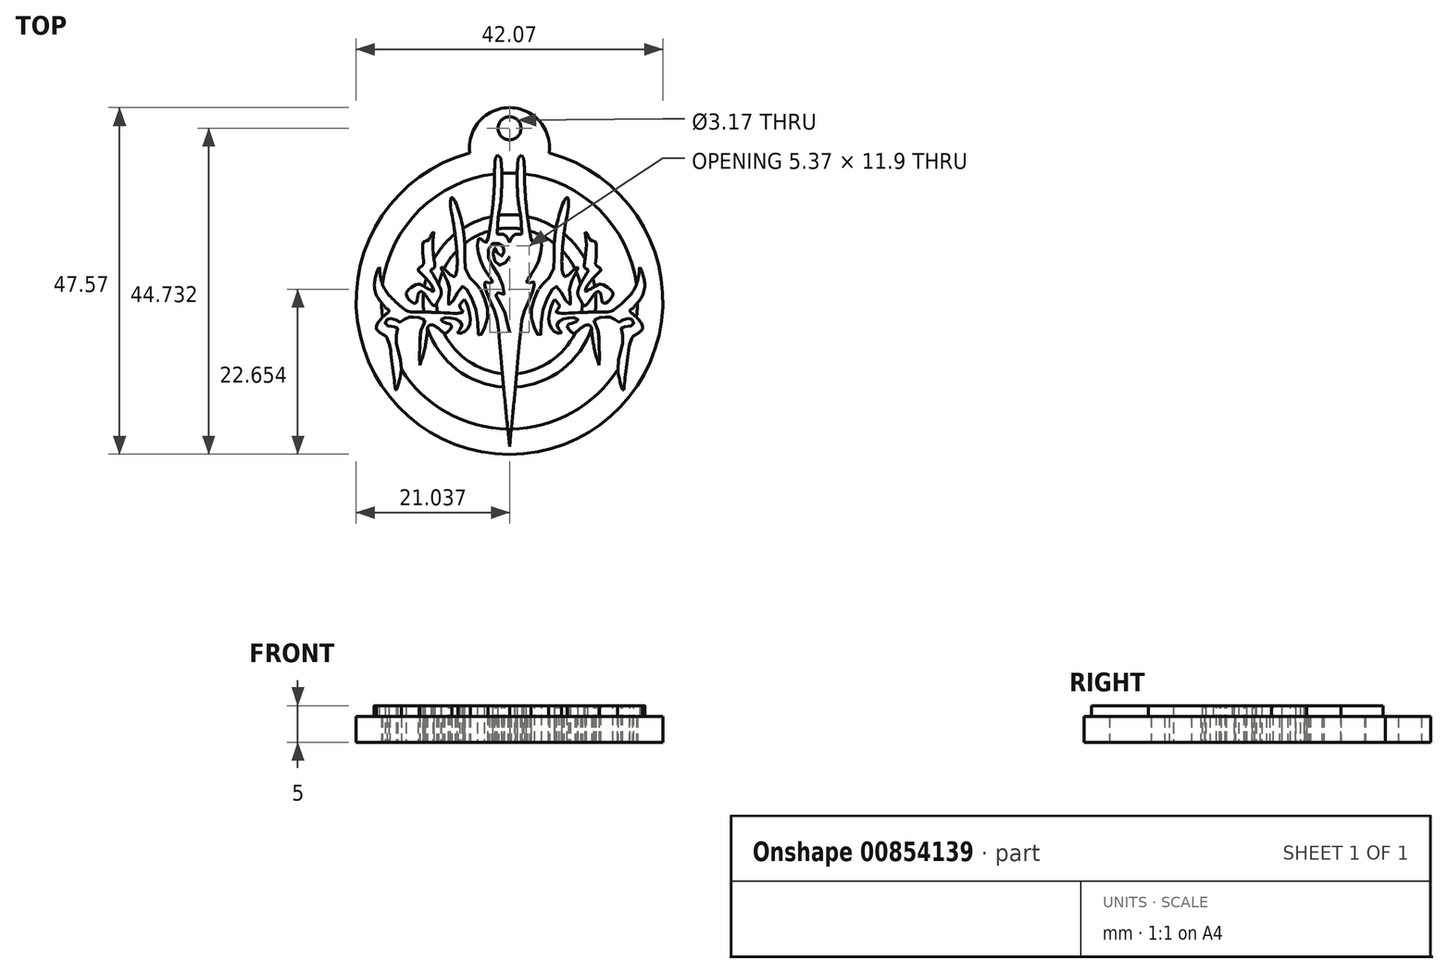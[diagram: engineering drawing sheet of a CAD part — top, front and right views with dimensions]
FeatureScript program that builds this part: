
annotation { "Feature Type Name" : "Feature", "Feature Type Description" : "" }
export const myFeature = defineFeature(function(context is Context, id is Id, definition is map)
    precondition{}
    {
        {
            var Q0;
            Q0=qCreatedBy(makeId("Top.planeOp"),FACE);
            var sketch = newSketch(context, id + "F0", { "sketchPlane" : qUnion([Q0])});
            skFitSpline(sketch, "E0", {"points": [v(-5.14, 14.8) * mm, v(-5.4, 14.38) * mm, v(-5.55, 11.82) * mm, v(-5.83, 7.5) * mm, v(-6.33, 3.87) * mm, v(-6.63, 2.9) * mm, v(-6.94, 2.82) * mm, v(-7.2, 3.15) * mm, v(-7.44, 3.37) * mm, v(-7.68, 3.39) * mm, v(-7.82, 3.07) * mm, v(-7.84, 1.76) * mm, v(-7.18, -0.34) * mm, v(-6.43, -1.55) * mm, v(-5.97, -2.28) * mm, v(-5.8, -2.52) * mm, v(-6.07, -2.72) * mm, v(-6.37, -2.66) * mm, v(-6.88, -2.6) * mm, v(-6.92, -2.8) * mm, v(-6.55, -4.2) * mm, v(-5.42, -7) * mm, v(-4.94, -9.94) * mm, v(-4.3, -17.1) * mm, v(-3.5, -25.2) * mm], "startDerivative": vector(-11.69, -12.68) * mm, "endDerivative": vector(7.97, -78.3) * mm});
            skFitSpline(sketch, "E1", {"points": [v(-5.14, 14.8) * mm, v(-4.8, 14.52) * mm, v(-4.6, 13.56) * mm, v(-4.54, 11.56) * mm, v(-4.58, 10.05) * mm, v(-4.73, 8.2) * mm, v(-5.05, 6.24) * mm, v(-5.14, 4.76) * mm, v(-5.14, 3.99) * mm, v(-4.51, 3.99) * mm, v(-3.91, 3.65) * mm, v(-3.5, 2.81) * mm], "startDerivative": vector(6.82, -3.82) * mm, "endDerivative": vector(4.35, -11.2) * mm});
            skFitSpline(sketch, "E2", {"points": [v(-3.5, 0.9) * mm, v(-3.76, 0.33) * mm, v(-4.4, -0.11) * mm, v(-4.9, -0.28) * mm, v(-5.3, -0.05) * mm, v(-5.66, 0.6) * mm, v(-5.76, 1.5) * mm, v(-5.6, 2.07) * mm, v(-5.36, 2) * mm, v(-5.14, 1.5) * mm, v(-4.86, 1.05) * mm, v(-4.55, 0.94) * mm, v(-4.33, 1.18) * mm, v(-4.26, 1.58) * mm, v(-4.26, 1.92) * mm, v(-4.44, 2.33) * mm, v(-4.73, 2.58) * mm, v(-5.14, 2.75) * mm, v(-5.6, 2.75) * mm, v(-6.1, 2.48) * mm, v(-6.4, 1.8) * mm, v(-6.43, 0.8) * mm, v(-5.94, -0.23) * mm, v(-5.05, -1.65) * mm, v(-4.4, -3.14) * mm, v(-4.22, -4.26) * mm, v(-4.46, -4.24) * mm, v(-5.05, -4.06) * mm, v(-5.39, -4.07) * mm, v(-5.33, -4.47) * mm, v(-4.74, -5.53) * mm, v(-4.08, -7.02) * mm, v(-3.73, -8.42) * mm, v(-3.5, -9.52) * mm], "startDerivative": vector(-6.13, -20.85) * mm, "endDerivative": vector(6, -27.3) * mm});
            skFitSpline(sketch, "E3", {"points": [v(-11.43, 9) * mm, v(-10.87, 8.29) * mm, v(-10.26, 6.48) * mm, v(-9.82, 4.42) * mm, v(-9.6, 1.1) * mm, v(-9.58, -0.72) * mm, v(-8.81, -2.15) * mm, v(-7.89, -3.02) * mm, v(-7.4, -3.67) * mm, v(-6.88, -4.98) * mm, v(-6.47, -6.43) * mm, v(-6.55, -7.66) * mm, v(-6.94, -8.97) * mm, v(-7.32, -9.77) * mm, v(-7.66, -10.04) * mm, v(-7.82, -8.9) * mm, v(-8.09, -6.45) * mm, v(-8.9, -4.43) * mm, v(-9.58, -3.32) * mm, v(-9.86, -3.16) * mm, v(-10.26, -3.46) * mm, v(-10.85, -4.51) * mm, v(-11.47, -5.44) * mm, v(-11.8, -5.68) * mm, v(-11.86, -5.18) * mm, v(-11.78, -4.1) * mm, v(-11.76, -3.2) * mm, v(-12.36, -1.83) * mm, v(-12.82, -0.78) * mm, v(-12.82, -0.58) * mm, v(-12.62, -0.64) * mm, v(-12, -1.23) * mm, v(-11.11, -1.83) * mm, v(-10.79, -1.33) * mm, v(-10.7, 1.43) * mm, v(-11.33, 6.33) * mm, v(-11.62, 8.13) * mm, v(-11.43, 9) * mm]});
            skFitSpline(sketch, "E4", {"points": [v(-13.9, 4.28) * mm, v(-14.39, 3.5) * mm, v(-14.65, 3.16) * mm, v(-15.3, 2.9) * mm, v(-15.4, 2.15) * mm, v(-15.37, 0.88) * mm, v(-15.28, 0) * mm, v(-15.4, -0.32) * mm, v(-16.04, -0.85) * mm, v(-15.73, -1.3) * mm, v(-14.92, -2.1) * mm, v(-14.3, -2.91) * mm, v(-13.96, -3.53) * mm, v(-13.9, -3.85) * mm, v(-14.39, -3.65) * mm, v(-15.42, -3.1) * mm, v(-15.97, -2.86) * mm, v(-16.64, -3.13) * mm, v(-17.46, -3.77) * mm, v(-17.67, -4.25) * mm, v(-17.2, -5.12) * mm, v(-16.52, -5.5) * mm, v(-16.26, -5.38) * mm, v(-16.07, -4.52) * mm, v(-15.85, -3.97) * mm, v(-15.54, -3.92) * mm, v(-15.08, -4.33) * mm, v(-14.48, -5.16) * mm, v(-13.86, -5.84) * mm, v(-13.57, -5.62) * mm, v(-12.95, -4.54) * mm, v(-12.93, -3.6) * mm, v(-13.6, -2.22) * mm, v(-14.15, -1.28) * mm, v(-14.27, -1) * mm, v(-13.96, -0.75) * mm, v(-13.77, -0.56) * mm, v(-13.89, 0.7) * mm, v(-14.03, 2.36) * mm, v(-13.98, 3.35) * mm, v(-13.9, 4.28) * mm]});
            skFitSpline(sketch, "E5", {"points": [v(-9.7, -5.01) * mm, v(-10.28, -5.67) * mm, v(-10.25, -6.15) * mm, v(-9.9, -6.64) * mm, v(-10.1, -6.8) * mm, v(-12.05, -6.84) * mm, v(-16.04, -6.7) * mm, v(-17.55, -6.52) * mm, v(-19.32, -5.13) * mm, v(-20.4, -3.93) * mm, v(-21.08, -2.36) * mm, v(-21.34, -0.54) * mm], "startDerivative": vector(-9.87, -9.17) * mm, "endDerivative": vector(-1.5, 17.66) * mm});
            skFitSpline(sketch, "E6", {"points": [v(-21.34, -0.54) * mm, v(-21.57, -0.9) * mm, v(-21.84, -1.76) * mm, v(-22.04, -2.85) * mm, v(-21.83, -4.23) * mm, v(-20.98, -5.54) * mm, v(-20.44, -6.14) * mm, v(-20.11, -6.39) * mm, v(-20.04, -6.6) * mm, v(-20.3, -6.89) * mm, v(-21.13, -7.64) * mm, v(-21.63, -8.4) * mm, v(-21.73, -9.04) * mm, v(-21.34, -9.47) * mm, v(-20.76, -9.84) * mm, v(-20.46, -10.03) * mm, v(-19.97, -11.13) * mm, v(-19.69, -13.16) * mm, v(-19.42, -15.28) * mm, v(-19.23, -16.75) * mm, v(-19.1, -17.42) * mm, v(-18.9, -17.13) * mm, v(-18.6, -16.03) * mm, v(-18.35, -14.5) * mm, v(-18.6, -12.58) * mm, v(-18.95, -11.25) * mm, v(-19.02, -9.93) * mm, v(-18.85, -8.93) * mm, v(-18.82, -8.8) * mm, v(-19.6, -8.75) * mm, v(-20.32, -8.57) * mm, v(-20.56, -8.3) * mm, v(-20.47, -7.88) * mm, v(-20.25, -7.7) * mm, v(-19.98, -7.62) * mm, v(-19.46, -7.62) * mm, v(-18.98, -7.82) * mm, v(-18.55, -8.07) * mm, v(-18.35, -8.02) * mm, v(-17.75, -7.62) * mm, v(-17.26, -7.41) * mm, v(-17.14, -7.41) * mm, v(-16.44, -7.43) * mm, v(-15.85, -7.47) * mm, v(-15.33, -7.67) * mm, v(-15.1, -7.85) * mm, v(-15.2, -8.2) * mm, v(-15.66, -9.35) * mm, v(-15.74, -9.9) * mm, v(-15.84, -12.25) * mm, v(-15.8, -13.99) * mm], "startDerivative": vector(-15.58, -21.3) * mm, "endDerivative": vector(2.34, -51.45) * mm});
            skFitSpline(sketch, "E7", {"points": [v(-15.8, -13.99) * mm, v(-15.41, -12.83) * mm, v(-15.05, -11.37) * mm, v(-14.9, -10.31) * mm, v(-14.78, -9.49) * mm, v(-14.7, -8.81) * mm, v(-14.4, -8.5) * mm, v(-13.93, -8.53) * mm, v(-13.4, -8.84) * mm, v(-13.04, -9.13) * mm, v(-12.93, -9.24) * mm, v(-12.62, -9.5) * mm, v(-12.45, -9.67) * mm, v(-12.16, -9.6) * mm, v(-11.81, -9.32) * mm, v(-11.5, -8.93) * mm, v(-11.42, -8.6) * mm, v(-11.59, -8.4) * mm, v(-12.06, -8.25) * mm, v(-12.64, -8.03) * mm, v(-12.93, -7.93) * mm, v(-12.68, -7.57) * mm, v(-11.91, -7.47) * mm, v(-11.1, -7.63) * mm, v(-10.42, -7.92) * mm, v(-10.04, -8.37) * mm, v(-10.2, -8.97) * mm, v(-10.61, -9.52) * mm, v(-10.5, -9.64) * mm, v(-9.94, -9.58) * mm, v(-9.39, -9.17) * mm, v(-9.07, -8.65) * mm, v(-8.88, -7.97) * mm, v(-9, -6.9) * mm, v(-9.25, -5.9) * mm, v(-9.55, -5.15) * mm, v(-9.7, -5.01) * mm], "startDerivative": vector(9.82, 27.15) * mm, "endDerivative": vector(-9.26, 5.8) * mm});
            skFitSpline(sketch, "E8.MirrorCS", {"points": [v(-1.84, 14.8) * mm, v(-2.19, 14.52) * mm, v(-2.38, 13.56) * mm, v(-2.45, 11.56) * mm, v(-2.4, 10.05) * mm, v(-2.26, 8.2) * mm, v(-1.94, 6.24) * mm, v(-1.84, 4.76) * mm, v(-1.84, 3.99) * mm, v(-2.48, 3.99) * mm, v(-3.07, 3.65) * mm, v(-3.5, 2.81) * mm], "startDerivative": vector(-6.82, -3.82) * mm, "endDerivative": vector(-4.35, -11.2) * mm});
            skFitSpline(sketch, "E9.MirrorCS", {"points": [v(-1.84, 14.8) * mm, v(-1.58, 14.38) * mm, v(-1.44, 11.82) * mm, v(-1.16, 7.5) * mm, v(-0.65, 3.87) * mm, v(-0.35, 2.9) * mm, v(-0.05, 2.82) * mm, v(0.21, 3.15) * mm, v(0.45, 3.37) * mm, v(0.7, 3.39) * mm, v(0.84, 3.07) * mm, v(0.86, 1.76) * mm, v(0.2, -0.34) * mm, v(-0.55, -1.55) * mm, v(-1.02, -2.28) * mm, v(-1.18, -2.52) * mm, v(-0.92, -2.72) * mm, v(-0.61, -2.66) * mm, v(-0.11, -2.6) * mm, v(-0.07, -2.8) * mm, v(-0.43, -4.2) * mm, v(-1.56, -7) * mm, v(-2.05, -9.94) * mm, v(-2.7, -17.1) * mm, v(-3.5, -25.2) * mm], "startDerivative": vector(11.69, -12.68) * mm, "endDerivative": vector(-7.97, -78.3) * mm});
            skFitSpline(sketch, "E10.MirrorCS", {"points": [v(-3.5, 0.9) * mm, v(-3.23, 0.33) * mm, v(-2.58, -0.11) * mm, v(-2.08, -0.28) * mm, v(-1.7, -0.05) * mm, v(-1.32, 0.6) * mm, v(-1.23, 1.5) * mm, v(-1.4, 2.07) * mm, v(-1.62, 2) * mm, v(-1.84, 1.5) * mm, v(-2.13, 1.05) * mm, v(-2.44, 0.94) * mm, v(-2.66, 1.18) * mm, v(-2.73, 1.58) * mm, v(-2.73, 1.92) * mm, v(-2.55, 2.33) * mm, v(-2.26, 2.58) * mm, v(-1.84, 2.75) * mm, v(-1.4, 2.75) * mm, v(-0.9, 2.48) * mm, v(-0.58, 1.8) * mm, v(-0.56, 0.8) * mm, v(-1.05, -0.23) * mm, v(-1.94, -1.65) * mm, v(-2.6, -3.14) * mm, v(-2.76, -4.26) * mm, v(-2.52, -4.24) * mm, v(-1.94, -4.06) * mm, v(-1.6, -4.07) * mm, v(-1.66, -4.47) * mm, v(-2.25, -5.53) * mm, v(-2.9, -7.02) * mm, v(-3.25, -8.42) * mm, v(-3.5, -9.52) * mm], "startDerivative": vector(6.13, -20.85) * mm, "endDerivative": vector(-6, -27.3) * mm});
            skFitSpline(sketch, "E11.MirrorC", {"points": [v(4.45, 9) * mm, v(3.88, 8.29) * mm, v(3.28, 6.48) * mm, v(2.83, 4.42) * mm, v(2.61, 1.1) * mm, v(2.6, -0.72) * mm, v(1.83, -2.15) * mm, v(0.9, -3.02) * mm, v(0.41, -3.67) * mm, v(-0.1, -4.98) * mm, v(-0.51, -6.43) * mm, v(-0.43, -7.66) * mm, v(-0.05, -8.97) * mm, v(0.33, -9.77) * mm, v(0.68, -10.04) * mm, v(0.84, -8.9) * mm, v(1.1, -6.45) * mm, v(1.9, -4.43) * mm, v(2.6, -3.32) * mm, v(2.87, -3.16) * mm, v(3.28, -3.46) * mm, v(3.86, -4.51) * mm, v(4.49, -5.44) * mm, v(4.8, -5.68) * mm, v(4.87, -5.18) * mm, v(4.79, -4.1) * mm, v(4.77, -3.2) * mm, v(5.37, -1.83) * mm, v(5.84, -0.78) * mm, v(5.84, -0.58) * mm, v(5.64, -0.64) * mm, v(5.01, -1.23) * mm, v(4.12, -1.83) * mm, v(3.8, -1.33) * mm, v(3.72, 1.43) * mm, v(4.35, 6.33) * mm, v(4.63, 8.13) * mm, v(4.45, 9) * mm]});
            skFitSpline(sketch, "E12.MirrorC", {"points": [v(6.92, 4.28) * mm, v(7.4, 3.5) * mm, v(7.67, 3.16) * mm, v(8.31, 2.9) * mm, v(8.4, 2.15) * mm, v(8.39, 0.88) * mm, v(8.29, 0) * mm, v(8.4, -0.32) * mm, v(9.06, -0.85) * mm, v(8.74, -1.3) * mm, v(7.93, -2.1) * mm, v(7.3, -2.91) * mm, v(6.97, -3.53) * mm, v(6.92, -3.85) * mm, v(7.4, -3.65) * mm, v(8.43, -3.1) * mm, v(8.98, -2.86) * mm, v(9.66, -3.13) * mm, v(10.47, -3.77) * mm, v(10.69, -4.25) * mm, v(10.2, -5.12) * mm, v(9.54, -5.5) * mm, v(9.27, -5.38) * mm, v(9.08, -4.52) * mm, v(8.86, -3.97) * mm, v(8.55, -3.92) * mm, v(8.1, -4.33) * mm, v(7.5, -5.16) * mm, v(6.87, -5.84) * mm, v(6.59, -5.62) * mm, v(5.96, -4.54) * mm, v(5.94, -3.6) * mm, v(6.61, -2.22) * mm, v(7.16, -1.28) * mm, v(7.28, -1) * mm, v(6.97, -0.75) * mm, v(6.78, -0.56) * mm, v(6.9, 0.7) * mm, v(7.04, 2.36) * mm, v(7, 3.35) * mm, v(6.92, 4.28) * mm]});
            skFitSpline(sketch, "E13.MirrorCS", {"points": [v(2.72, -5.01) * mm, v(3.3, -5.67) * mm, v(3.26, -6.15) * mm, v(2.92, -6.64) * mm, v(3.12, -6.8) * mm, v(5.06, -6.84) * mm, v(9.05, -6.7) * mm, v(10.56, -6.52) * mm, v(12.33, -5.13) * mm, v(13.41, -3.93) * mm, v(14.1, -2.36) * mm, v(14.35, -0.54) * mm], "startDerivative": vector(9.87, -9.17) * mm, "endDerivative": vector(1.5, 17.66) * mm});
            skFitSpline(sketch, "E14.MirrorCS", {"points": [v(14.35, -0.54) * mm, v(14.58, -0.9) * mm, v(14.85, -1.76) * mm, v(15.05, -2.85) * mm, v(14.84, -4.23) * mm, v(14, -5.54) * mm, v(13.45, -6.14) * mm, v(13.13, -6.39) * mm, v(13.05, -6.6) * mm, v(13.3, -6.89) * mm, v(14.14, -7.64) * mm, v(14.65, -8.4) * mm, v(14.75, -9.04) * mm, v(14.35, -9.47) * mm, v(13.77, -9.84) * mm, v(13.47, -10.03) * mm, v(12.98, -11.13) * mm, v(12.7, -13.16) * mm, v(12.43, -15.28) * mm, v(12.24, -16.75) * mm, v(12.1, -17.42) * mm, v(11.92, -17.13) * mm, v(11.62, -16.03) * mm, v(11.36, -14.5) * mm, v(11.6, -12.58) * mm, v(11.97, -11.25) * mm, v(12.04, -9.93) * mm, v(11.87, -8.93) * mm, v(11.83, -8.8) * mm, v(12.6, -8.75) * mm, v(13.33, -8.57) * mm, v(13.57, -8.3) * mm, v(13.48, -7.88) * mm, v(13.26, -7.7) * mm, v(13, -7.62) * mm, v(12.47, -7.62) * mm, v(12, -7.82) * mm, v(11.56, -8.07) * mm, v(11.37, -8.02) * mm, v(10.76, -7.62) * mm, v(10.27, -7.41) * mm, v(10.16, -7.41) * mm, v(9.46, -7.43) * mm, v(8.87, -7.47) * mm, v(8.35, -7.67) * mm, v(8.11, -7.85) * mm, v(8.2, -8.2) * mm, v(8.67, -9.35) * mm, v(8.75, -9.9) * mm, v(8.85, -12.25) * mm, v(8.82, -13.99) * mm], "startDerivative": vector(15.58, -21.3) * mm, "endDerivative": vector(-2.34, -51.45) * mm});
            skFitSpline(sketch, "E15.MirrorCS", {"points": [v(8.82, -13.99) * mm, v(8.42, -12.83) * mm, v(8.07, -11.37) * mm, v(7.91, -10.31) * mm, v(7.8, -9.49) * mm, v(7.72, -8.81) * mm, v(7.4, -8.5) * mm, v(6.95, -8.53) * mm, v(6.42, -8.84) * mm, v(6.05, -9.13) * mm, v(5.94, -9.24) * mm, v(5.63, -9.5) * mm, v(5.46, -9.67) * mm, v(5.17, -9.6) * mm, v(4.82, -9.32) * mm, v(4.52, -8.93) * mm, v(4.43, -8.6) * mm, v(4.6, -8.4) * mm, v(5.07, -8.25) * mm, v(5.65, -8.03) * mm, v(5.94, -7.93) * mm, v(5.7, -7.57) * mm, v(4.92, -7.47) * mm, v(4.1, -7.63) * mm, v(3.43, -7.92) * mm, v(3.05, -8.37) * mm, v(3.2, -8.97) * mm, v(3.63, -9.52) * mm, v(3.51, -9.64) * mm, v(2.96, -9.58) * mm, v(2.4, -9.17) * mm, v(2.08, -8.65) * mm, v(1.9, -7.97) * mm, v(2, -6.9) * mm, v(2.27, -5.9) * mm, v(2.56, -5.15) * mm, v(2.72, -5.01) * mm], "startDerivative": vector(-9.82, 27.15) * mm, "endDerivative": vector(9.26, 5.8) * mm});
            skCircle(sketch, "E16", {"center": v(-3.5, -5.2) * mm, "radius": 11.85 * mm});
            skCircle(sketch, "E17", {"center": v(-3.5, -5.2) * mm, "radius": 10 * mm});
            skCircle(sketch, "E18", {"center": v(-3.5, -5.2) * mm, "radius": 21.04 * mm});
            skArc(sketch, "E19", {"start": v(-21.05, -5.46) * mm, "mid": v(-21, -6.44) * mm, "end": v(-20.91, -7.42) * mm});
            skArc(sketch, "E20.trimOffspring", {"start": v(-20.32, -10.22) * mm, "mid": v(-20.11, -10.86) * mm, "end": v(-19.89, -11.49) * mm});
            skArc(sketch, "E21.trimOffspring", {"start": v(-18.35, -14.56) * mm, "mid": v(13.66, -1.43) * mm, "end": v(-20.9, -2.93) * mm});
            skCircle(sketch, "E22", {"center": v(-3.5, 18.5) * mm, "radius": 1.59 * mm});
            skPoint(sketch, "E23.center.orphan", {"position": v(-3.5, 15.84) * mm});
            skArc(sketch, "E24.trimOffspring", {"start": v(1.96, 15.12) * mm, "mid": v(-3.5, 21.34) * mm, "end": v(-8.95, 15.12) * mm});
            skSolve(sketch);
        }
        {
            var Q0;
            Q0 = qSketchRegion(id + "F0", true);
            var Q1;
            {var subQ0=sQuery(id+"F0.wireOp",EDGE,"E16");var subQ1=sQuery(id+"F0.wireOp",EDGE,"E0");var subQ2=makeQuery(id+"F0.imprint","INTERSECT",VERTEX,{"disambiguationData":[OD(0.0)],"derivedFrom":[subQ1,subQ0]});Q1=makeQuery(id+"F0.imprint","IMPRINT",FACE,{"disambiguationData":[TD([[makeQuery(id+"F0.imprint","IMPRINT",EDGE,{"disambiguationData":[TD([[subQ2,-1.0]])],"derivedFrom":subQ1}),-1.0]])]});}
            var Q2;
            {var subQ0=sQuery(id+"F0.wireOp",EDGE,"E16");var subQ1=sQuery(id+"F0.wireOp",EDGE,"E1");var subQ2=makeQuery(id+"F0.imprint","INTERSECT",VERTEX,{"derivedFrom":[subQ1,subQ0]});Q2=makeQuery(id+"F0.imprint","IMPRINT",FACE,{"disambiguationData":[TD([[makeQuery(id+"F0.imprint","IMPRINT",EDGE,{"disambiguationData":[TD([[subQ2,-1.0]])],"derivedFrom":subQ1}),1.0]])]});}
            var Q3;
            {var subQ0=sQuery(id+"F0.wireOp",EDGE,"E16");var subQ1=sQuery(id+"F0.wireOp",EDGE,"E9.MirrorCS");var subQ2=makeQuery(id+"F0.imprint","INTERSECT",VERTEX,{"disambiguationData":[OD(0.0)],"derivedFrom":[subQ1,subQ0]});Q3=makeQuery(id+"F0.imprint","IMPRINT",FACE,{"disambiguationData":[TD([[makeQuery(id+"F0.imprint","IMPRINT",EDGE,{"disambiguationData":[TD([[subQ2,-1.0]])],"derivedFrom":subQ1}),1.0]])]});}
            var Q4;
            {var subQ1=sQuery(id+"F0.wireOp",EDGE,"E11.MirrorC");var subQ5=sQuery(id+"F0.wireOp",EDGE,"E17");var subQ8=makeQuery(id+"F0.imprint","INTERSECT",VERTEX,{"disambiguationData":[OD(1.0)],"derivedFrom":[subQ1,subQ5]});Q4=makeQuery(id+"F0.imprint","IMPRINT",FACE,{"disambiguationData":[TD([[makeQuery(id+"F0.imprint","IMPRINT",EDGE,{"disambiguationData":[TD([[subQ8,-1.0]])],"derivedFrom":subQ1}),-1.0]])]});}
            var Q5;
            {var subQ0=sQuery(id+"F0.wireOp",EDGE,"E16");var subQ1=sQuery(id+"F0.wireOp",EDGE,"E12.MirrorC");var subQ2=makeQuery(id+"F0.imprint","INTERSECT",VERTEX,{"disambiguationData":[OD(2.0)],"derivedFrom":[subQ1,subQ0]});Q5=makeQuery(id+"F0.imprint","IMPRINT",FACE,{"disambiguationData":[TD([[makeQuery(id+"F0.imprint","IMPRINT",EDGE,{"disambiguationData":[TD([[subQ2,-1.0]])],"derivedFrom":subQ1}),1.0]])]});}
            var Q6;
            {var subQ0=sQuery(id+"F0.wireOp",EDGE,"E17");var subQ1=sQuery(id+"F0.wireOp",EDGE,"E9.MirrorCS");var subQ2=makeQuery(id+"F0.imprint","INTERSECT",VERTEX,{"disambiguationData":[OD(1.0)],"derivedFrom":[subQ1,subQ0]});Q6=makeQuery(id+"F0.imprint","IMPRINT",FACE,{"disambiguationData":[TD([[makeQuery(id+"F0.imprint","IMPRINT",EDGE,{"disambiguationData":[TD([[subQ2,-1.0]])],"derivedFrom":subQ1}),1.0]])]});}
            var Q7;
            {var subQ0=sQuery(id+"F0.wireOp",EDGE,"E17");var subQ1=sQuery(id+"F0.wireOp",EDGE,"E0");var subQ2=makeQuery(id+"F0.imprint","INTERSECT",VERTEX,{"disambiguationData":[OD(1.0)],"derivedFrom":[subQ1,subQ0]});Q7=makeQuery(id+"F0.imprint","IMPRINT",FACE,{"disambiguationData":[TD([[makeQuery(id+"F0.imprint","IMPRINT",EDGE,{"disambiguationData":[TD([[subQ2,-1.0]])],"derivedFrom":subQ1}),-1.0]])]});}
            var Q8;
            {var subQ0=sQuery(id+"F0.wireOp",EDGE,"E16");var subQ1=sQuery(id+"F0.wireOp",EDGE,"E4");var subQ2=makeQuery(id+"F0.imprint","INTERSECT",VERTEX,{"disambiguationData":[OD(2.0)],"derivedFrom":[subQ1,subQ0]});Q8=makeQuery(id+"F0.imprint","IMPRINT",FACE,{"disambiguationData":[TD([[makeQuery(id+"F0.imprint","IMPRINT",EDGE,{"disambiguationData":[TD([[subQ2,-1.0]])],"derivedFrom":subQ1}),-1.0]])]});}
            var Q9;
            {var subQ0=sQuery(id+"F0.wireOp",EDGE,"E16");var subQ1=sQuery(id+"F0.wireOp",EDGE,"E4");var subQ2=makeQuery(id+"F0.imprint","INTERSECT",VERTEX,{"disambiguationData":[OD(0.0)],"derivedFrom":[subQ1,subQ0]});Q9=makeQuery(id+"F0.imprint","IMPRINT",FACE,{"disambiguationData":[TD([[makeQuery(id+"F0.imprint","IMPRINT",EDGE,{"disambiguationData":[TD([[subQ2,1.0]])],"derivedFrom":subQ1}),-1.0]])]});}
            var Q10;
            {var subQ1=sQuery(id+"F0.wireOp",EDGE,"E3");var subQ5=sQuery(id+"F0.wireOp",EDGE,"E17");var subQ8=makeQuery(id+"F0.imprint","INTERSECT",VERTEX,{"disambiguationData":[OD(1.0)],"derivedFrom":[subQ1,subQ5]});Q10=makeQuery(id+"F0.imprint","IMPRINT",FACE,{"disambiguationData":[TD([[makeQuery(id+"F0.imprint","IMPRINT",EDGE,{"disambiguationData":[TD([[subQ8,-1.0]])],"derivedFrom":subQ1}),1.0]])]});}
            var Q11;
            {var subQ0=sQuery(id+"F0.wireOp",EDGE,"E16");var subQ1=sQuery(id+"F0.wireOp",EDGE,"E12.MirrorC");var subQ2=makeQuery(id+"F0.imprint","INTERSECT",VERTEX,{"disambiguationData":[OD(0.0)],"derivedFrom":[subQ1,subQ0]});Q11=makeQuery(id+"F0.imprint","IMPRINT",FACE,{"disambiguationData":[TD([[makeQuery(id+"F0.imprint","IMPRINT",EDGE,{"disambiguationData":[TD([[subQ2,1.0]])],"derivedFrom":subQ1}),1.0]])]});}
            extrude(context, id + "F1", {"entities" : qUnion([Q0, Q1, Q2, Q3, Q4, Q5, Q6, Q7, Q8, Q9, Q10, Q11]), "depth" : 3.5 * mm, "offsetDistance" : 25 * mm});
        }
        {
            var Q0;
            {var subQ0=sQuery(id+"F0.wireOp",EDGE,"E21.trimOffspring");var subQ1=sQuery(id+"F0.wireOp",EDGE,"E0");var subQ2=makeQuery(id+"F0.imprint","INTERSECT",VERTEX,{"disambiguationData":[OD(0.0)],"derivedFrom":[subQ1,subQ0]});Q0=makeQuery(id+"F0.imprint","IMPRINT",FACE,{"disambiguationData":[TD([[makeQuery(id+"F0.imprint","IMPRINT",EDGE,{"disambiguationData":[TD([[subQ2,-1.0]])],"derivedFrom":subQ1}),1.0]])]});}
            var Q1;
            {var subQ0=sQuery(id+"F0.wireOp",EDGE,"E1");var subQ1=sQuery(id+"F0.wireOp",EDGE,"E0");var subQ2=makeQuery(id+"F0.imprint","INTERSECT",VERTEX,{"derivedFrom":[subQ1,subQ0]});Q1=makeQuery(id+"F0.imprint","IMPRINT",FACE,{"disambiguationData":[TD([[makeQuery(id+"F0.imprint","IMPRINT",EDGE,{"disambiguationData":[TD([[subQ2,-1.0]])],"derivedFrom":subQ1}),1.0]])]});}
            var Q2;
            {var subQ0=sQuery(id+"F0.wireOp",EDGE,"E9.MirrorCS");var subQ1=sQuery(id+"F0.wireOp",EDGE,"E8.MirrorCS");var subQ2=makeQuery(id+"F0.imprint","INTERSECT",VERTEX,{"derivedFrom":[subQ1,subQ0]});Q2=makeQuery(id+"F0.imprint","IMPRINT",FACE,{"disambiguationData":[TD([[makeQuery(id+"F0.imprint","IMPRINT",EDGE,{"disambiguationData":[TD([[subQ2,-1.0]])],"derivedFrom":subQ1}),1.0]])]});}
            var Q3;
            {var subQ0=sQuery(id+"F0.wireOp",EDGE,"E21.trimOffspring");var subQ1=sQuery(id+"F0.wireOp",EDGE,"E8.MirrorCS");var subQ2=makeQuery(id+"F0.imprint","INTERSECT",VERTEX,{"derivedFrom":[subQ1,subQ0]});Q3=makeQuery(id+"F0.imprint","IMPRINT",FACE,{"disambiguationData":[TD([[makeQuery(id+"F0.imprint","IMPRINT",EDGE,{"disambiguationData":[TD([[subQ2,-1.0]])],"derivedFrom":subQ1}),1.0]])]});}
            var Q4;
            {var subQ0=sQuery(id+"F0.wireOp",EDGE,"E16");var subQ1=sQuery(id+"F0.wireOp",EDGE,"E0");var subQ2=makeQuery(id+"F0.imprint","INTERSECT",VERTEX,{"disambiguationData":[OD(0.0)],"derivedFrom":[subQ1,subQ0]});Q4=makeQuery(id+"F0.imprint","IMPRINT",FACE,{"disambiguationData":[TD([[makeQuery(id+"F0.imprint","IMPRINT",EDGE,{"disambiguationData":[TD([[subQ2,-1.0]])],"derivedFrom":subQ1}),1.0]])]});}
            var Q5;
            Q5=makeQuery(id+"F0.imprint","IMPRINT",FACE,{"disambiguationData":[TD([[makeQuery(id+"F0.imprint","IMPRINT",EDGE,{"derivedFrom":sQuery(id+"F0.wireOp",EDGE,"E2")}),-1.0]])]});
            var Q6;
            {var subQ0=sQuery(id+"F0.wireOp",EDGE,"E16");var subQ1=sQuery(id+"F0.wireOp",EDGE,"E8.MirrorCS");var subQ2=makeQuery(id+"F0.imprint","INTERSECT",VERTEX,{"derivedFrom":[subQ1,subQ0]});Q6=makeQuery(id+"F0.imprint","IMPRINT",FACE,{"disambiguationData":[TD([[makeQuery(id+"F0.imprint","IMPRINT",EDGE,{"disambiguationData":[TD([[subQ2,-1.0]])],"derivedFrom":subQ1}),1.0]])]});}
            var Q7;
            {var subQ0=sQuery(id+"F0.wireOp",EDGE,"E17");var subQ1=sQuery(id+"F0.wireOp",EDGE,"E5");var subQ2=makeQuery(id+"F0.imprint","INTERSECT",VERTEX,{"derivedFrom":[subQ1,subQ0]});Q7=makeQuery(id+"F0.imprint","IMPRINT",FACE,{"disambiguationData":[TD([[makeQuery(id+"F0.imprint","IMPRINT",EDGE,{"disambiguationData":[TD([[subQ2,-1.0]])],"derivedFrom":subQ1}),1.0]])]});}
            var Q8;
            {var subQ0=sQuery(id+"F0.wireOp",EDGE,"E7");var subQ1=sQuery(id+"F0.wireOp",EDGE,"E5");var subQ2=makeQuery(id+"F0.imprint","INTERSECT",VERTEX,{"derivedFrom":[subQ1,subQ0]});Q8=makeQuery(id+"F0.imprint","IMPRINT",FACE,{"disambiguationData":[TD([[makeQuery(id+"F0.imprint","IMPRINT",EDGE,{"disambiguationData":[TD([[subQ2,-1.0]])],"derivedFrom":subQ1}),1.0]])]});}
            var Q9;
            {var subQ4=sQuery(id+"F0.wireOp",EDGE,"E5");var subQ6=sQuery(id+"F0.wireOp",EDGE,"E21.trimOffspring");var subQ7=makeQuery(id+"F0.imprint","INTERSECT",VERTEX,{"derivedFrom":[subQ4,subQ6]});Q9=makeQuery(id+"F0.imprint","IMPRINT",FACE,{"disambiguationData":[TD([[makeQuery(id+"F0.imprint","IMPRINT",EDGE,{"disambiguationData":[TD([[subQ7,1.0]])],"derivedFrom":subQ4}),1.0]])]});}
            var Q10;
            {var subQ0=sQuery(id+"F0.wireOp",EDGE,"E16");var subQ1=sQuery(id+"F0.wireOp",EDGE,"E4");var subQ2=makeQuery(id+"F0.imprint","INTERSECT",VERTEX,{"disambiguationData":[OD(0.0)],"derivedFrom":[subQ1,subQ0]});Q10=makeQuery(id+"F0.imprint","IMPRINT",FACE,{"disambiguationData":[TD([[makeQuery(id+"F0.imprint","IMPRINT",EDGE,{"disambiguationData":[TD([[subQ2,-1.0]])],"derivedFrom":subQ1}),1.0]])]});}
            var Q11;
            {var subQ0=sQuery(id+"F0.wireOp",EDGE,"E16");var subQ1=sQuery(id+"F0.wireOp",EDGE,"E4");var subQ2=makeQuery(id+"F0.imprint","INTERSECT",VERTEX,{"disambiguationData":[OD(1.0)],"derivedFrom":[subQ1,subQ0]});Q11=makeQuery(id+"F0.imprint","IMPRINT",FACE,{"disambiguationData":[TD([[makeQuery(id+"F0.imprint","IMPRINT",EDGE,{"disambiguationData":[TD([[subQ2,1.0]])],"derivedFrom":subQ1}),1.0]])]});}
            var Q12;
            {var subQ0=sQuery(id+"F0.wireOp",EDGE,"E17");var subQ1=sQuery(id+"F0.wireOp",EDGE,"E0");var subQ2=makeQuery(id+"F0.imprint","INTERSECT",VERTEX,{"disambiguationData":[OD(1.0)],"derivedFrom":[subQ1,subQ0]});Q12=makeQuery(id+"F0.imprint","IMPRINT",FACE,{"disambiguationData":[TD([[makeQuery(id+"F0.imprint","IMPRINT",EDGE,{"disambiguationData":[TD([[subQ2,-1.0]])],"derivedFrom":subQ1}),1.0]])]});}
            var Q13;
            {var subQ0=sQuery(id+"F0.wireOp",EDGE,"E16");var subQ1=sQuery(id+"F0.wireOp",EDGE,"E0");var subQ2=makeQuery(id+"F0.imprint","INTERSECT",VERTEX,{"disambiguationData":[OD(1.0)],"derivedFrom":[subQ1,subQ0]});Q13=makeQuery(id+"F0.imprint","IMPRINT",FACE,{"disambiguationData":[TD([[makeQuery(id+"F0.imprint","IMPRINT",EDGE,{"disambiguationData":[TD([[subQ2,-1.0]])],"derivedFrom":subQ1}),1.0]])]});}
            var Q14;
            {var subQ0=sQuery(id+"F0.wireOp",EDGE,"E9.MirrorCS");var subQ1=sQuery(id+"F0.wireOp",EDGE,"E0");var subQ2=makeQuery(id+"F0.imprint","INTERSECT",VERTEX,{"derivedFrom":[subQ1,subQ0]});Q14=makeQuery(id+"F0.imprint","IMPRINT",FACE,{"disambiguationData":[TD([[makeQuery(id+"F0.imprint","IMPRINT",EDGE,{"disambiguationData":[TD([[subQ2,1.0]])],"derivedFrom":subQ1}),1.0]])]});}
            var Q15;
            {var subQ0=sQuery(id+"F0.wireOp",EDGE,"E21.trimOffspring");var subQ1=sQuery(id+"F0.wireOp",EDGE,"E14.MirrorCS");var subQ2=makeQuery(id+"F0.imprint","INTERSECT",VERTEX,{"disambiguationData":[OD(3.0)],"derivedFrom":[subQ1,subQ0]});Q15=makeQuery(id+"F0.imprint","IMPRINT",FACE,{"disambiguationData":[TD([[makeQuery(id+"F0.imprint","IMPRINT",EDGE,{"disambiguationData":[TD([[subQ2,-1.0]])],"derivedFrom":subQ1}),-1.0]])]});}
            var Q16;
            {var subQ9=sQuery(id+"F0.wireOp",EDGE,"E16");var subQ10=sQuery(id+"F0.wireOp",EDGE,"E13.MirrorCS");var subQ11=makeQuery(id+"F0.imprint","INTERSECT",VERTEX,{"derivedFrom":[subQ10,subQ9]});Q16=makeQuery(id+"F0.imprint","IMPRINT",FACE,{"disambiguationData":[TD([[makeQuery(id+"F0.imprint","IMPRINT",EDGE,{"disambiguationData":[TD([[subQ11,-1.0]])],"derivedFrom":subQ10}),-1.0]])]});}
            var Q17;
            {var subQ0=sQuery(id+"F0.wireOp",EDGE,"E14.MirrorCS");var subQ1=sQuery(id+"F0.wireOp",EDGE,"E13.MirrorCS");var subQ2=makeQuery(id+"F0.imprint","INTERSECT",VERTEX,{"derivedFrom":[subQ1,subQ0]});Q17=makeQuery(id+"F0.imprint","IMPRINT",FACE,{"disambiguationData":[TD([[makeQuery(id+"F0.imprint","IMPRINT",EDGE,{"disambiguationData":[TD([[subQ2,1.0]])],"derivedFrom":subQ1}),-1.0]])]});}
            var Q18;
            {var subQ0=sQuery(id+"F0.wireOp",EDGE,"E21.trimOffspring");var subQ1=sQuery(id+"F0.wireOp",EDGE,"E14.MirrorCS");var subQ2=makeQuery(id+"F0.imprint","INTERSECT",VERTEX,{"disambiguationData":[OD(1.0)],"derivedFrom":[subQ1,subQ0]});Q18=makeQuery(id+"F0.imprint","IMPRINT",FACE,{"disambiguationData":[TD([[makeQuery(id+"F0.imprint","IMPRINT",EDGE,{"disambiguationData":[TD([[subQ2,-1.0]])],"derivedFrom":subQ1}),-1.0]])]});}
            var Q19;
            {var subQ0=sQuery(id+"F0.wireOp",EDGE,"E17");var subQ1=sQuery(id+"F0.wireOp",EDGE,"E13.MirrorCS");var subQ2=makeQuery(id+"F0.imprint","INTERSECT",VERTEX,{"derivedFrom":[subQ1,subQ0]});Q19=makeQuery(id+"F0.imprint","IMPRINT",FACE,{"disambiguationData":[TD([[makeQuery(id+"F0.imprint","IMPRINT",EDGE,{"disambiguationData":[TD([[subQ2,-1.0]])],"derivedFrom":subQ1}),-1.0]])]});}
            var Q20;
            {var subQ0=sQuery(id+"F0.wireOp",EDGE,"E16");var subQ1=sQuery(id+"F0.wireOp",EDGE,"E12.MirrorC");var subQ2=makeQuery(id+"F0.imprint","INTERSECT",VERTEX,{"disambiguationData":[OD(0.0)],"derivedFrom":[subQ1,subQ0]});Q20=makeQuery(id+"F0.imprint","IMPRINT",FACE,{"disambiguationData":[TD([[makeQuery(id+"F0.imprint","IMPRINT",EDGE,{"disambiguationData":[TD([[subQ2,1.0]])],"derivedFrom":subQ1}),-1.0]])]});}
            var Q21;
            {var subQ0=sQuery(id+"F0.wireOp",EDGE,"E16");var subQ1=sQuery(id+"F0.wireOp",EDGE,"E12.MirrorC");var subQ2=makeQuery(id+"F0.imprint","INTERSECT",VERTEX,{"disambiguationData":[OD(0.0)],"derivedFrom":[subQ1,subQ0]});Q21=makeQuery(id+"F0.imprint","IMPRINT",FACE,{"disambiguationData":[TD([[makeQuery(id+"F0.imprint","IMPRINT",EDGE,{"disambiguationData":[TD([[subQ2,-1.0]])],"derivedFrom":subQ1}),-1.0]])]});}
            var Q22;
            {var subQ0=sQuery(id+"F0.wireOp",EDGE,"E16");var subQ1=sQuery(id+"F0.wireOp",EDGE,"E12.MirrorC");var subQ2=makeQuery(id+"F0.imprint","INTERSECT",VERTEX,{"disambiguationData":[OD(1.0)],"derivedFrom":[subQ1,subQ0]});Q22=makeQuery(id+"F0.imprint","IMPRINT",FACE,{"disambiguationData":[TD([[makeQuery(id+"F0.imprint","IMPRINT",EDGE,{"disambiguationData":[TD([[subQ2,1.0]])],"derivedFrom":subQ1}),-1.0]])]});}
            var Q23;
            {var subQ0=sQuery(id+"F0.wireOp",EDGE,"E17");var subQ1=sQuery(id+"F0.wireOp",EDGE,"E12.MirrorC");var subQ2=makeQuery(id+"F0.imprint","INTERSECT",VERTEX,{"disambiguationData":[OD(0.0)],"derivedFrom":[subQ1,subQ0]});Q23=makeQuery(id+"F0.imprint","IMPRINT",FACE,{"disambiguationData":[TD([[makeQuery(id+"F0.imprint","IMPRINT",EDGE,{"disambiguationData":[TD([[subQ2,-1.0]])],"derivedFrom":subQ1}),-1.0]])]});}
            var Q24;
            {var subQ0=sQuery(id+"F0.wireOp",EDGE,"E15.MirrorCS");var subQ1=sQuery(id+"F0.wireOp",EDGE,"E13.MirrorCS");var subQ2=makeQuery(id+"F0.imprint","INTERSECT",VERTEX,{"derivedFrom":[subQ1,subQ0]});Q24=makeQuery(id+"F0.imprint","IMPRINT",FACE,{"disambiguationData":[TD([[makeQuery(id+"F0.imprint","IMPRINT",EDGE,{"disambiguationData":[TD([[subQ2,-1.0]])],"derivedFrom":subQ1}),-1.0]])]});}
            var Q25;
            {var subQ0=sQuery(id+"F0.wireOp",EDGE,"E17");var subQ1=sQuery(id+"F0.wireOp",EDGE,"E11.MirrorC");var subQ2=makeQuery(id+"F0.imprint","INTERSECT",VERTEX,{"disambiguationData":[OD(0.0)],"derivedFrom":[subQ1,subQ0]});Q25=makeQuery(id+"F0.imprint","IMPRINT",FACE,{"disambiguationData":[TD([[makeQuery(id+"F0.imprint","IMPRINT",EDGE,{"disambiguationData":[TD([[subQ2,-1.0]])],"derivedFrom":subQ1}),1.0]])]});}
            var Q26;
            {var subQ0=sQuery(id+"F0.wireOp",EDGE,"E17");var subQ1=sQuery(id+"F0.wireOp",EDGE,"E11.MirrorC");var subQ2=makeQuery(id+"F0.imprint","INTERSECT",VERTEX,{"disambiguationData":[OD(0.0)],"derivedFrom":[subQ1,subQ0]});Q26=makeQuery(id+"F0.imprint","IMPRINT",FACE,{"disambiguationData":[TD([[makeQuery(id+"F0.imprint","IMPRINT",EDGE,{"disambiguationData":[TD([[subQ2,1.0]])],"derivedFrom":subQ1}),1.0]])]});}
            var Q27;
            {var subQ0=sQuery(id+"F0.wireOp",EDGE,"E16");var subQ1=sQuery(id+"F0.wireOp",EDGE,"E11.MirrorC");var subQ2=makeQuery(id+"F0.imprint","INTERSECT",VERTEX,{"disambiguationData":[OD(0.0)],"derivedFrom":[subQ1,subQ0]});Q27=makeQuery(id+"F0.imprint","IMPRINT",FACE,{"disambiguationData":[TD([[makeQuery(id+"F0.imprint","IMPRINT",EDGE,{"disambiguationData":[TD([[subQ2,1.0]])],"derivedFrom":subQ1}),1.0]])]});}
            var Q28;
            {var subQ0=sQuery(id+"F0.wireOp",EDGE,"E16");var subQ1=sQuery(id+"F0.wireOp",EDGE,"E3");var subQ2=makeQuery(id+"F0.imprint","INTERSECT",VERTEX,{"disambiguationData":[OD(0.0)],"derivedFrom":[subQ1,subQ0]});Q28=makeQuery(id+"F0.imprint","IMPRINT",FACE,{"disambiguationData":[TD([[makeQuery(id+"F0.imprint","IMPRINT",EDGE,{"disambiguationData":[TD([[subQ2,1.0]])],"derivedFrom":subQ1}),-1.0]])]});}
            var Q29;
            {var subQ0=sQuery(id+"F0.wireOp",EDGE,"E17");var subQ1=sQuery(id+"F0.wireOp",EDGE,"E3");var subQ2=makeQuery(id+"F0.imprint","INTERSECT",VERTEX,{"disambiguationData":[OD(0.0)],"derivedFrom":[subQ1,subQ0]});Q29=makeQuery(id+"F0.imprint","IMPRINT",FACE,{"disambiguationData":[TD([[makeQuery(id+"F0.imprint","IMPRINT",EDGE,{"disambiguationData":[TD([[subQ2,1.0]])],"derivedFrom":subQ1}),-1.0]])]});}
            var Q30;
            {var subQ0=sQuery(id+"F0.wireOp",EDGE,"E17");var subQ1=sQuery(id+"F0.wireOp",EDGE,"E3");var subQ2=makeQuery(id+"F0.imprint","INTERSECT",VERTEX,{"disambiguationData":[OD(0.0)],"derivedFrom":[subQ1,subQ0]});Q30=makeQuery(id+"F0.imprint","IMPRINT",FACE,{"disambiguationData":[TD([[makeQuery(id+"F0.imprint","IMPRINT",EDGE,{"disambiguationData":[TD([[subQ2,-1.0]])],"derivedFrom":subQ1}),-1.0]])]});}
            var Q31;
            {var subQ0=sQuery(id+"F0.wireOp",EDGE,"E17");var subQ1=sQuery(id+"F0.wireOp",EDGE,"E11.MirrorC");var subQ2=makeQuery(id+"F0.imprint","INTERSECT",VERTEX,{"disambiguationData":[OD(1.0)],"derivedFrom":[subQ1,subQ0]});Q31=makeQuery(id+"F0.imprint","IMPRINT",FACE,{"disambiguationData":[TD([[makeQuery(id+"F0.imprint","IMPRINT",EDGE,{"disambiguationData":[TD([[subQ2,-1.0]])],"derivedFrom":subQ1}),1.0]])]});}
            var Q32;
            {var subQ0=sQuery(id+"F0.wireOp",EDGE,"E17");var subQ1=sQuery(id+"F0.wireOp",EDGE,"E3");var subQ2=makeQuery(id+"F0.imprint","INTERSECT",VERTEX,{"disambiguationData":[OD(1.0)],"derivedFrom":[subQ1,subQ0]});Q32=makeQuery(id+"F0.imprint","IMPRINT",FACE,{"disambiguationData":[TD([[makeQuery(id+"F0.imprint","IMPRINT",EDGE,{"disambiguationData":[TD([[subQ2,-1.0]])],"derivedFrom":subQ1}),-1.0]])]});}
            var Q33;
            {var subQ0=sQuery(id+"F0.wireOp",EDGE,"E16");var subQ1=sQuery(id+"F0.wireOp",EDGE,"E4");var subQ8=makeQuery(id+"F0.imprint","INTERSECT",VERTEX,{"disambiguationData":[OD(0.0)],"derivedFrom":[subQ1,subQ0]});Q33=makeQuery(id+"F0.imprint","IMPRINT",FACE,{"disambiguationData":[TD([[makeQuery(id+"F0.imprint","IMPRINT",EDGE,{"disambiguationData":[TD([[subQ8,1.0]])],"derivedFrom":subQ1}),1.0]])]});}
            var Q34;
            {var subQ0=sQuery(id+"F0.wireOp",EDGE,"E17");var subQ1=sQuery(id+"F0.wireOp",EDGE,"E4");var subQ2=makeQuery(id+"F0.imprint","INTERSECT",VERTEX,{"disambiguationData":[OD(0.0)],"derivedFrom":[subQ1,subQ0]});Q34=makeQuery(id+"F0.imprint","IMPRINT",FACE,{"disambiguationData":[TD([[makeQuery(id+"F0.imprint","IMPRINT",EDGE,{"disambiguationData":[TD([[subQ2,-1.0]])],"derivedFrom":subQ1}),1.0]])]});}
            extrude(context, id + "F2", {"entities" : qUnion([Q0, Q1, Q2, Q3, Q4, Q5, Q6, Q7, Q8, Q9, Q10, Q11, Q12, Q13, Q14, Q15, Q16, Q17, Q18, Q19, Q20, Q21, Q22, Q23, Q24, Q25, Q26, Q27, Q28, Q29, Q30, Q31, Q32, Q33, Q34]), "operationType" : NewBodyOperationType.ADD, "depth" : 5 * mm, "offsetDistance" : 25 * mm});
        }
    });
